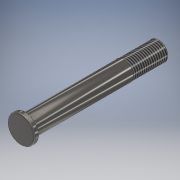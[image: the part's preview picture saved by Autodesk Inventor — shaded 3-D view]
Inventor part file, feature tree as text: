
AUTODESK INVENTOR PART (.ipt)
format: ipt  version: 2019 (Build 230136000, 136)  size: 128,000 bytes
history: native  units: mm
features: other x1, revolve x1, fillet x1, chamfer x1, thread x1, sketch x1
ambient origin geometry x8: Origin, YZ Plane, XZ Plane, XY Plane, X Axis, Y Axis, Z Axis, Center Point
bodies: Body1 (feature_tree)
feature tree (6):
  other  "Твердое тело1"
  revolve  "Вращение1"
  fillet  "Сопряжение1"  Radius=64.0mm
  chamfer  "Фаска1"  Distance=9.3mm
  thread  "Thread1"  [1 undecoded]
  sketch  "Эскиз1"
note: 1 required parameter value undecoded (feature->parameter linkage not recoverable at this tier; creation-order binding heuristic only, values carry confidence <= 0.55)
